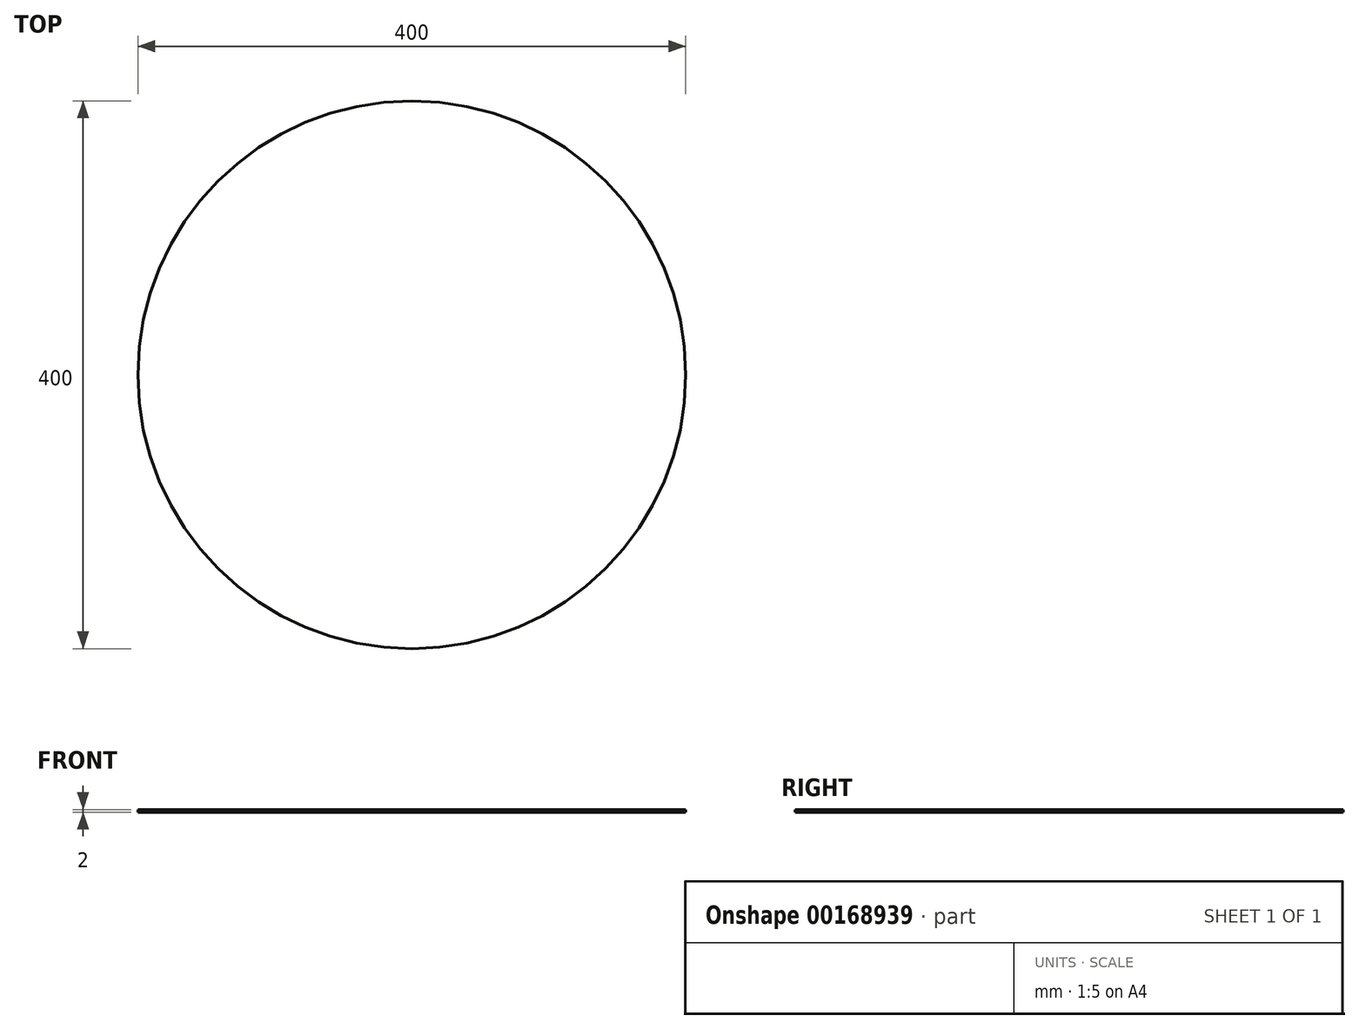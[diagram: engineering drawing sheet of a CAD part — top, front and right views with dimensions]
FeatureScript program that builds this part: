
annotation { "Feature Type Name" : "Feature", "Feature Type Description" : "" }
export const myFeature = defineFeature(function(context is Context, id is Id, definition is map)
    precondition{}
    {
        {
            var Q0;
            Q0=qCreatedBy(makeId("Top.planeOp"),FACE);
            var sketch = newSketch(context, id + "F0", { "sketchPlane" : qUnion([Q0])});
            skCircle(sketch, "E0", {"center": v(0, 0) * mm, "radius": 200 * mm});
            skCircle(sketch, "E1", {"center": v(0, 0) * mm, "radius": 204 * mm});
            skSolve(sketch);
        }
        {
            var Q0;
            Q0=sQuery(id+"F0.wireOp",EDGE,"E1");
            extrude(context, id + "F1", {"bodyType" : ToolBodyType.SURFACE, "surfaceEntities" : qUnion([Q0]), "oppositeDirection" : true, "depth" : 600 * mm});
        }
        {
            var Q0;
            Q0=makeQuery(id+"F0.imprint","IMPRINT",FACE,{"disambiguationData":[TD([[makeQuery(id+"F0.imprint","IMPRINT",EDGE,{"derivedFrom":sQuery(id+"F0.wireOp",EDGE,"E0")}),1.0]])]});
            extrude(context, id + "F2", {"entities" : qUnion([Q0]), "oppositeDirection" : true, "depth" : 102 * mm});
        }
        {
            var Q0;
            Q0=makeQuery(id+"F0.imprint","IMPRINT",FACE,{"disambiguationData":[TD([[makeQuery(id+"F0.imprint","IMPRINT",EDGE,{"derivedFrom":sQuery(id+"F0.wireOp",EDGE,"E0")}),1.0]])]});
            extrude(context, id + "F3", {"entities" : qUnion([Q0]), "operationType" : NewBodyOperationType.REMOVE, "oppositeDirection" : true, "depth" : 100 * mm});
        }
    });
